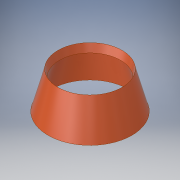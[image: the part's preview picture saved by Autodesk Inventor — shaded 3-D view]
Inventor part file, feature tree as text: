
AUTODESK INVENTOR PART (.ipt)
format: ipt  version: 2017 SP1 (Build 210196100, 196)  size: 151,552 bytes
history: native  units: in
note: dims shown in document units (in); Inventor stores cm internally (conversion verified against a paired STEP export)
features: revolve x1, sketch x1
ambient origin geometry x8: Origin, YZ Plane, XZ Plane, XY Plane, X Axis, Y Axis, Z Axis, Center Point
bodies: Body1 (feature_tree)
feature tree (2):
  revolve  "Revolution3"  [1 undecoded]
  sketch  "Sketch1"  dims[d0=1.13in d3=0.1718in d5=1.0in d6=1.0in d7=90.0deg d8=0.5in d9=15.0deg d31=0.25in d34=15.0deg d37=1.75in d40=3.75in d41=0.125in d46=0.75in d47=0.5in d51=0.5in d52=0.25in d54=0.5in d55=0.5in d56=1.25in d58=0.0017in d59=0.5in d60=0.5in d61=1.0in d62=0.234in d63=0.234in d64=0.125in d67=0.25in d68=4.25in d69=0.25in d70=0.25in d71=0.125in d73=3.4in d74=1.25in d75=0.2498in d77=90.0deg]
note: 1 required parameter value undecoded (feature->parameter linkage not recoverable at this tier; creation-order binding heuristic only, values carry confidence <= 0.55)
